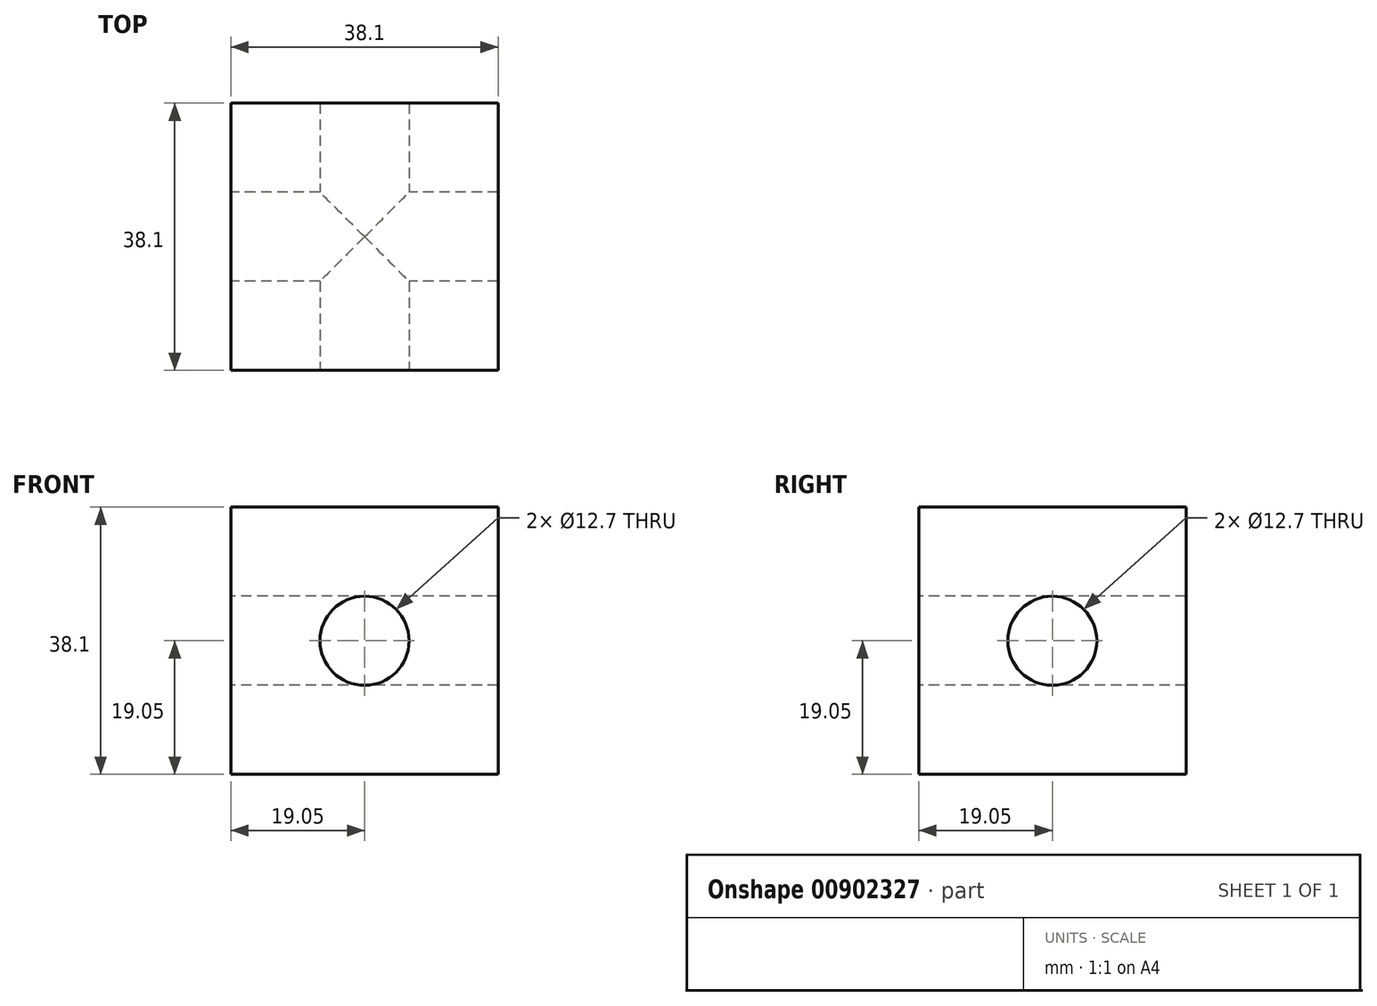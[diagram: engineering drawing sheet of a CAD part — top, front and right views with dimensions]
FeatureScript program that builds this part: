
annotation { "Feature Type Name" : "Feature", "Feature Type Description" : "" }
export const myFeature = defineFeature(function(context is Context, id is Id, definition is map)
    precondition{}
    {
        {
            var Q0;
            Q0=qCreatedBy(makeId("Front.planeOp"),FACE);
            var sketch = newSketch(context, id + "F0", { "sketchPlane" : qUnion([Q0])});
            skLineSegment(sketch, "E0.bottom", {"start": v(-19.05, 19.05) * mm, "end": v(19.05, 19.05) * mm});
            skLineSegment(sketch, "E0.top", {"start": v(-19.05, -19.05) * mm, "end": v(19.05, -19.05) * mm});
            skLineSegment(sketch, "E0.left", {"start": v(-19.05, 19.05) * mm, "end": v(-19.05, -19.05) * mm});
            skLineSegment(sketch, "E0.right", {"start": v(19.05, 19.05) * mm, "end": v(19.05, -19.05) * mm});
            skPoint(sketch, "E0.middle", {"position": v(0, 0) * mm});
            skSolve(sketch);
        }
        {
            var Q0;
            Q0=makeQuery(id+"F0.imprint","IMPRINT",FACE,{"disambiguationData":[TD([[makeQuery(id+"F0.imprint","IMPRINT",EDGE,{"derivedFrom":sQuery(id+"F0.wireOp",EDGE,"E0.bottom")}),-1.0]])]});
            extrude(context, id + "F1", {"entities" : qUnion([Q0]), "endBound" : BoundingType.SYMMETRIC, "depth" : 38.1 * mm, "offsetDistance" : 25.4 * mm});
        }
        {
            var Q0;
            Q0=makeQuery(id+"F1.opExtrude","CAP_FACE",FACE,{"disambiguationData":[OSD([sQuery(id+"F0.wireOp",EDGE,"E0.bottom"),sQuery(id+"F0.wireOp",EDGE,"E0.top"),sQuery(id+"F0.wireOp",EDGE,"E0.left"),sQuery(id+"F0.wireOp",EDGE,"E0.right")])],"isStart":false});
            var sketch = newSketch(context, id + "F2", { "sketchPlane" : qUnion([Q0])});
            skPoint(sketch, "E1", {"position": v(0, 0) * mm});
            skSolve(sketch);
        }
        {
            var Q0;
            Q0=makeQuery(id+"F1.opExtrude","SWEPT_FACE",FACE,{"disambiguationData":[OSD([sQuery(id+"F0.wireOp",EDGE,"E0.left")])]});
            var sketch = newSketch(context, id + "F3", { "sketchPlane" : qUnion([Q0])});
            skPoint(sketch, "E2", {"position": v(0, 0) * mm});
            skSolve(sketch);
        }
        {
            var Q0;
            Q0=sQuery(id+"F2.wireOp",VERTEX,"E1");
            var Q1;
            Q1=sQuery(id+"F3.wireOp",VERTEX,"E2");
            var Q2;
            Q2=makeQuery(id+"F1.opExtrude","SWEPT_BODY",BODY,{"disambiguationData":[OSD([sQuery(id+"F0.wireOp",EDGE,"E0.bottom"),sQuery(id+"F0.wireOp",EDGE,"E0.top"),sQuery(id+"F0.wireOp",EDGE,"E0.left"),sQuery(id+"F0.wireOp",EDGE,"E0.right")])]});
            hole(context, id + "F4", {"style" : HoleStyle.SIMPLE, "endStyle" : HoleEndStyle.THROUGH, "holeDiameter" : 12.7 * mm, "majorDiameter" : 6.35 * mm, "isTappedThrough" : true, "tappedDepth" : 12.7 * mm, "tapClearance" : 3, "locations" : qUnion([Q0, Q1]), "scope" : qUnion([Q2])});
        }
    });
